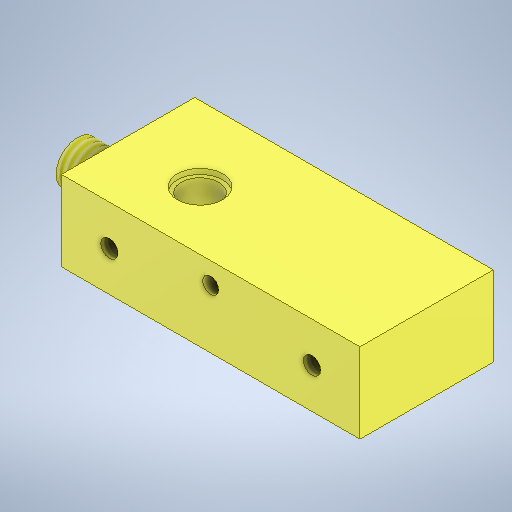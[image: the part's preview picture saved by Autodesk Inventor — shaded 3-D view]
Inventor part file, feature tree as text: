
AUTODESK INVENTOR PART (.ipt)
format: ipt  version: 2025.1 (Build 291241000, 241)  size: 306,176 bytes
history: native  units: mm
features: sketch x8, hole x3, extrude x2, plane x2, revolve x1, thread x1, sweep x1, projected_geometry x1
ambient origin geometry x8: Origin, YZ Plane, XZ Plane, XY Plane, X Axis, Y Axis, Z Axis, Center Point
bodies: Solid1 (feature_tree)
feature tree (19):
  extrude  "Extrusion1"  Depth=25.0mm
  hole  "Hole1"  [1 undecoded]
  plane  "Work Plane1"
  revolve  "Revolution1"  [1 undecoded]
  hole  "Hole2"  [1 undecoded]
  thread  "Thread1"  [1 undecoded]
  hole  "Hole3"  [1 undecoded]
  plane  "Work Plane3"
  sweep  "Sweep1"
  extrude  "Extrusion2"  Depth=38.0mm
  sketch  "Sketch1"  dims[d0=56.0mm d1=25.0mm]
  sketch  "Sketch2"  dims[d2=15.0mm d3=0.0mm d4=11.0mm]
  sketch  "Sketch3"  dims[d5=15.0mm]
  sketch  "Sketch4"  dims[d6=7.0mm d7=6.0mm d8=8.5mm d9=1.0mm d10=90.0deg d11=3.5mm d12=0.0mm d13=0.0mm]
  sketch  "Sketch6"  dims[d14=8.0mm d15=11.0mm d16=3.0mm]
  sketch  "Sketch8"  dims[d17=11.0mm d18=10.0mm]
  sketch  "Sketch10"  dims[d19=90.0deg]
  sketch  "Sketch12"  dims[d20=5.0mm d21=6.0mm d22=8.5mm d23=1.0mm d24=90.0deg d25=11.0mm d26=0.0mm d27=8.0mm d28=0.0mm d29=38.0mm d30=19.0mm d31=3.242mm d32=5.0mm d33=5.0mm d34=9.0mm d35=90.0deg d36=5.0mm d37=0.0mm d39=-28.0mm d40=5.2mm d41=4.0mm d42=3.0mm d43=0.0mm d44=0.0mm d45=3.0mm d46=11.0mm d47=32.0mm d48=0.0mm]
  projected_geometry  "Projected Loop1"
note: 5 required parameter values undecoded (feature->parameter linkage not recoverable at this tier; creation-order binding heuristic only, values carry confidence <= 0.55)